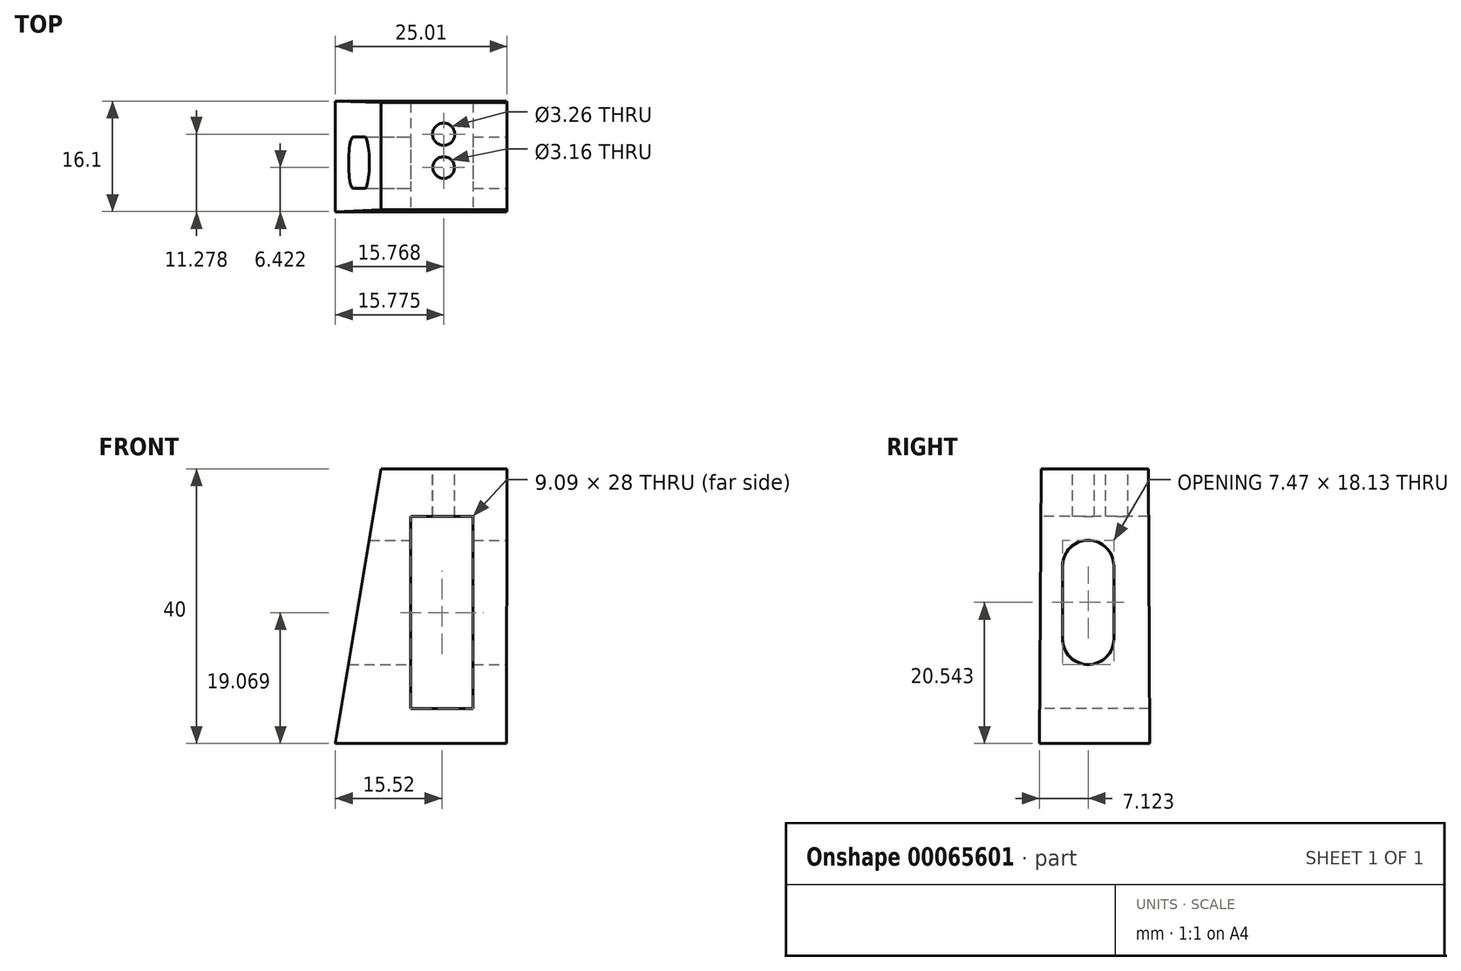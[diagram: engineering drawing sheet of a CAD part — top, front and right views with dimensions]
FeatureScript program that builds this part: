
annotation { "Feature Type Name" : "Feature", "Feature Type Description" : "" }
export const myFeature = defineFeature(function(context is Context, id is Id, definition is map)
    precondition{}
    {
        {
            var Q0;
            Q0=qCreatedBy(makeId("Top.planeOp"),FACE);
            cPlane(context, id + "F0", {"entities" : qUnion([Q0]), "cplaneType" : CPlaneType.OFFSET, "offset" : 40 * mm, "width" : 150 * mm, "height" : 150 * mm});
        }
        {
            var Q0;
            Q0=qCreatedBy(makeId("Top.planeOp"),FACE);
            var sketch = newSketch(context, id + "F1", { "sketchPlane" : qUnion([Q0])});
            skLineSegment(sketch, "E0.bottom", {"start": v(-48.69, 22.44) * mm, "end": v(-23.79, 22.44) * mm});
            skLineSegment(sketch, "E0.top", {"start": v(-48.69, 38.54) * mm, "end": v(-23.79, 38.54) * mm});
            skLineSegment(sketch, "E0.left", {"start": v(-48.69, 22.44) * mm, "end": v(-48.69, 38.54) * mm});
            skLineSegment(sketch, "E0.right", {"start": v(-23.79, 22.44) * mm, "end": v(-23.79, 38.54) * mm});
            skSolve(sketch);
        }
        {
            var Q0;
            Q0=qCreatedBy(id+"F0.planeOp",FACE);
            var sketch = newSketch(context, id + "F2", { "sketchPlane" : qUnion([Q0])});
            skLineSegment(sketch, "E1.bottom", {"start": v(-42.02, 38.34) * mm, "end": v(-23.68, 38.34) * mm});
            skLineSegment(sketch, "E1.top", {"start": v(-42.02, 22.74) * mm, "end": v(-23.68, 22.74) * mm});
            skLineSegment(sketch, "E1.left", {"start": v(-42.02, 38.34) * mm, "end": v(-42.02, 22.74) * mm});
            skLineSegment(sketch, "E1.right", {"start": v(-23.68, 38.34) * mm, "end": v(-23.68, 22.74) * mm});
            skSolve(sketch);
        }
        {
            var Q0;
            Q0=makeQuery(id+"F1.imprint","IMPRINT",FACE,{"disambiguationData":[TD([[makeQuery(id+"F1.imprint","IMPRINT",EDGE,{"derivedFrom":sQuery(id+"F1.wireOp",EDGE,"E0.bottom")}),1.0]])]});
            var Q1;
            Q1=makeQuery(id+"F2.imprint","IMPRINT",FACE,{"disambiguationData":[TD([[makeQuery(id+"F2.imprint","IMPRINT",EDGE,{"derivedFrom":sQuery(id+"F2.wireOp",EDGE,"E1.bottom")}),-1.0]])]});
            loft(context, id + "F3", {"sheetProfilesArray" : [{ "sheetProfileEntities" : qUnion([Q0]) }, { "sheetProfileEntities" : qUnion([Q1]) }]});
        }
        {
            var Q0;
            Q0=qCreatedBy(makeId("Front.planeOp"),FACE);
            var sketch = newSketch(context, id + "F4", { "sketchPlane" : qUnion([Q0])});
            skLineSegment(sketch, "E2.bottom", {"start": v(-37.71, 33.07) * mm, "end": v(-28.62, 33.07) * mm});
            skLineSegment(sketch, "E2.top", {"start": v(-37.71, 5.07) * mm, "end": v(-28.62, 5.07) * mm});
            skLineSegment(sketch, "E2.left", {"start": v(-37.71, 33.07) * mm, "end": v(-37.71, 5.07) * mm});
            skLineSegment(sketch, "E2.right", {"start": v(-28.62, 33.07) * mm, "end": v(-28.62, 5.07) * mm});
            skSolve(sketch);
        }
        {
            var Q0;
            Q0 = qSketchRegion(id + "F4", true);
            extrude(context, id + "F5", {"entities" : qUnion([Q0]), "operationType" : NewBodyOperationType.REMOVE, "oppositeDirection" : true, "depth" : 43.98 * mm});
        }
        {
            var Q0;
            Q0=qCreatedBy(makeId("Right.planeOp"),FACE);
            var sketch = newSketch(context, id + "F6", { "sketchPlane" : qUnion([Q0])});
            skLineSegment(sketch, "E3", {"start": v(25.83, 25.87) * mm, "end": v(25.83, 15.21) * mm});
            skLineSegment(sketch, "E4", {"start": v(33.3, 25.87) * mm, "end": v(33.3, 15.21) * mm});
            skArc(sketch, "E5", {"start": v(33.3, 25.87) * mm, "mid": v(29.56, 29.6) * mm, "end": v(25.83, 25.87) * mm});
            skArc(sketch, "E6", {"start": v(25.83, 15.21) * mm, "mid": v(29.56, 11.48) * mm, "end": v(33.3, 15.21) * mm});
            skSolve(sketch);
        }
        {
            var Q0;
            Q0 = qSketchRegion(id + "F6", true);
            extrude(context, id + "F7", {"entities" : qUnion([Q0]), "operationType" : NewBodyOperationType.REMOVE, "oppositeDirection" : true, "depth" : 48.6 * mm});
        }
        {
            var Q0;
            Q0=qCreatedBy(id+"F0.planeOp",FACE);
            var sketch = newSketch(context, id + "F8", { "sketchPlane" : qUnion([Q0])});
            skCircle(sketch, "E7", {"center": v(-32.91, 33.72) * mm, "radius": 1.63 * mm});
            skSolve(sketch);
        }
        {
            var Q0;
            Q0 = qSketchRegion(id + "F8", true);
            extrude(context, id + "F9", {"entities" : qUnion([Q0]), "operationType" : NewBodyOperationType.REMOVE, "oppositeDirection" : true, "depth" : 25 * mm});
        }
        {
            var Q0;
            Q0=qCreatedBy(id+"F0.planeOp",FACE);
            var sketch = newSketch(context, id + "F10", { "sketchPlane" : qUnion([Q0])});
            skCircle(sketch, "E8", {"center": v(-32.92, 28.86) * mm, "radius": 1.58 * mm});
            skSolve(sketch);
        }
        {
            var Q0;
            Q0 = qSketchRegion(id + "F10", true);
            extrude(context, id + "F11", {"entities" : qUnion([Q0]), "operationType" : NewBodyOperationType.REMOVE, "oppositeDirection" : true, "depth" : 25 * mm});
        }
    });
